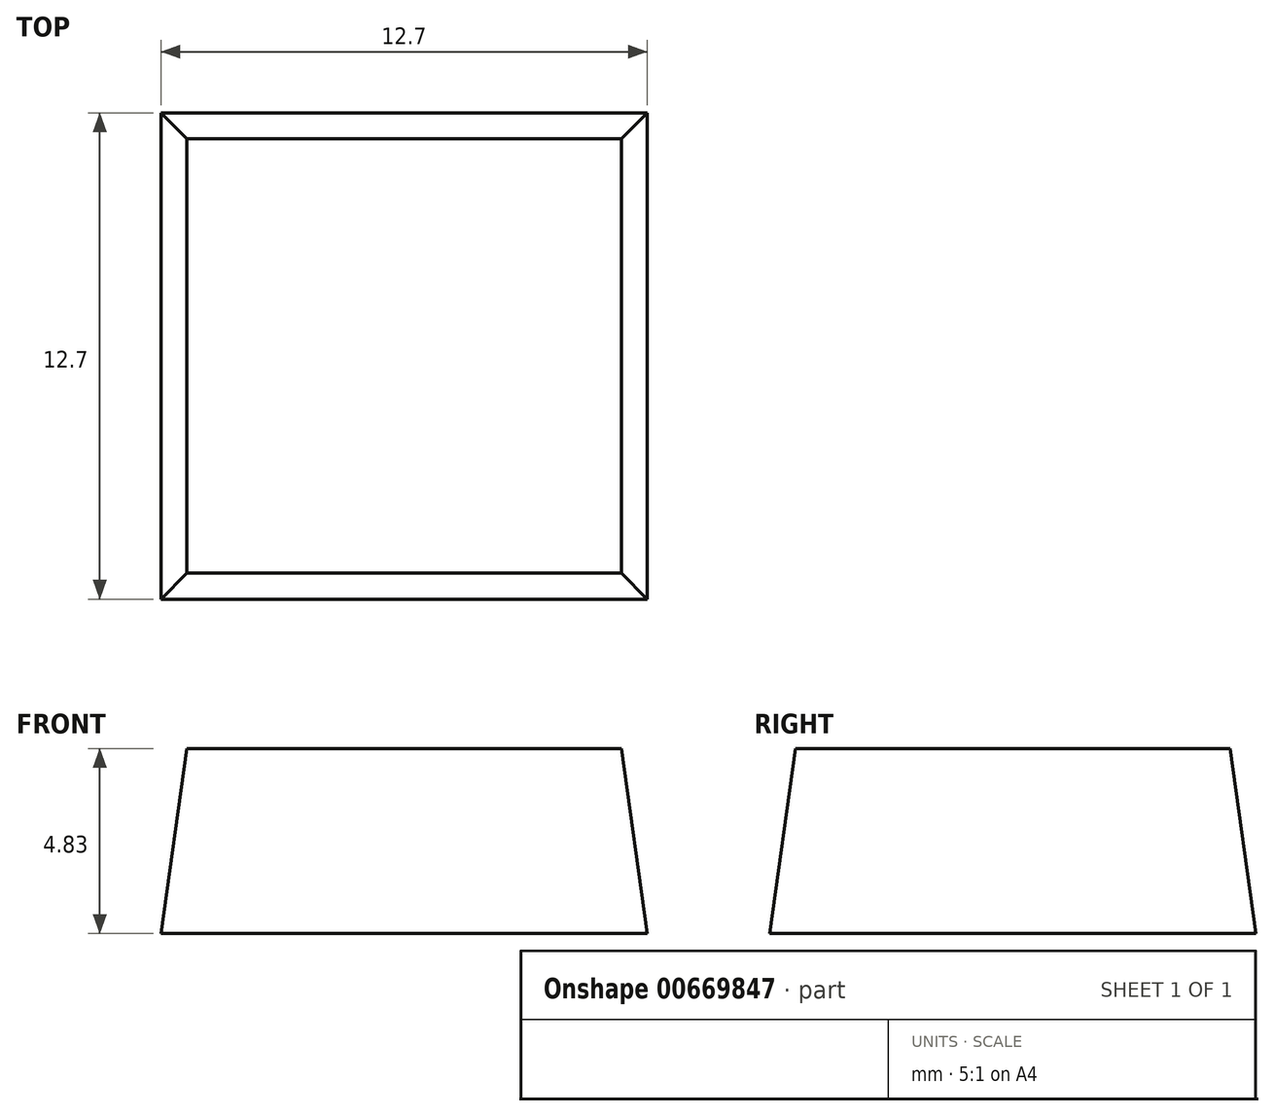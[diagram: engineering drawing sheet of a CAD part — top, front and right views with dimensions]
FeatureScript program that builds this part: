
annotation { "Feature Type Name" : "Feature", "Feature Type Description" : "" }
export const myFeature = defineFeature(function(context is Context, id is Id, definition is map)
    precondition{}
    {
        {
            var Q0;
            Q0=qCreatedBy(makeId("Top.planeOp"),FACE);
            var sketch = newSketch(context, id + "F0", { "sketchPlane" : qUnion([Q0])});
            skLineSegment(sketch, "E0.bottom", {"start": v(0, 0) * mm, "end": v(12.7, 0) * mm});
            skLineSegment(sketch, "E0.top", {"start": v(0, 12.7) * mm, "end": v(12.7, 12.7) * mm});
            skLineSegment(sketch, "E0.left", {"start": v(0, 0) * mm, "end": v(0, 12.7) * mm});
            skLineSegment(sketch, "E0.right", {"start": v(12.7, 0) * mm, "end": v(12.7, 12.7) * mm});
            skSolve(sketch);
        }
        {
            var Q0;
            Q0 = qSketchRegion(id + "F0", true);
            extrude(context, id + "F1", {"entities" : qUnion([Q0]), "depth" : 4.83 * mm, "offsetDistance" : 25.4 * mm, "hasDraft" : true, "draftAngle" : 8 * degree, "draftPullDirection" : true});
        }
    });
